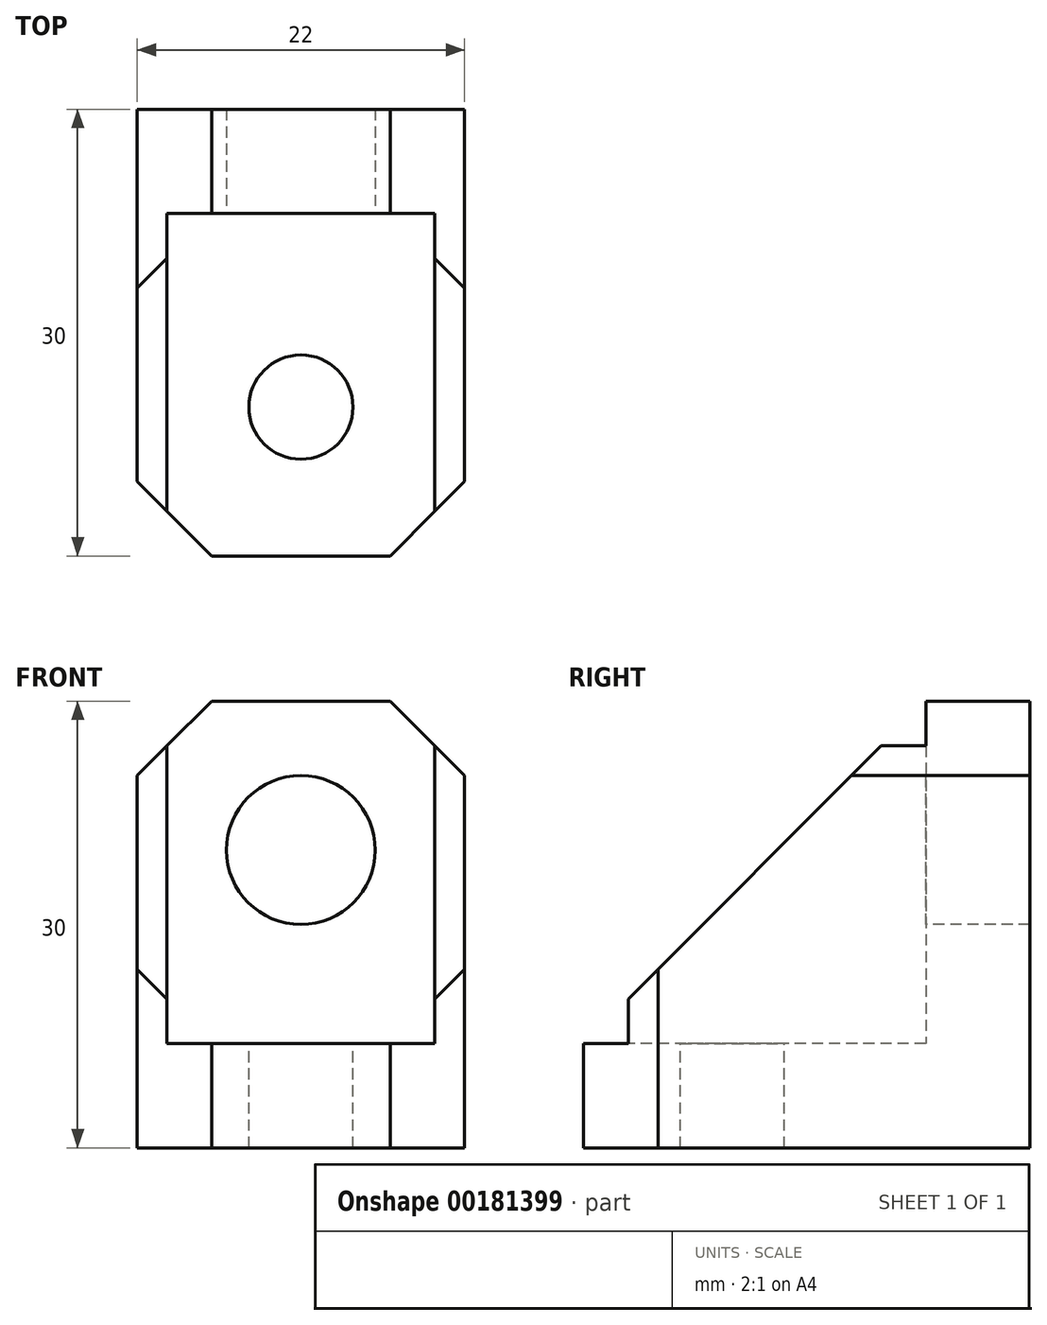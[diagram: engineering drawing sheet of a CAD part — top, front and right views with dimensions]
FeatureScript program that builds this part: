
annotation { "Feature Type Name" : "Feature", "Feature Type Description" : "" }
export const myFeature = defineFeature(function(context is Context, id is Id, definition is map)
    precondition{}
    {
        {
            var Q0;
            Q0=qCreatedBy(makeId("Top.planeOp"),FACE);
            var sketch = newSketch(context, id + "F0", { "sketchPlane" : qUnion([Q0])});
            skLineSegment(sketch, "E0.bottom", {"start": v(11, -15) * mm, "end": v(-11, -15) * mm});
            skLineSegment(sketch, "E0.top", {"start": v(11, 15) * mm, "end": v(-11, 15) * mm});
            skLineSegment(sketch, "E0.left", {"start": v(11, -15) * mm, "end": v(11, 15) * mm});
            skLineSegment(sketch, "E0.right", {"start": v(-11, -15) * mm, "end": v(-11, 15) * mm});
            skPoint(sketch, "E0.middle", {"position": v(0, 0) * mm});
            skLineSegment(sketch, "E1", {"start": v(-11, 8) * mm, "end": v(11, 8) * mm});
            skLineSegment(sketch, "E2", {"start": v(-11, 5) * mm, "end": v(11, 5) * mm, "construction": true});
            skCircle(sketch, "E3", {"center": v(0, -5) * mm, "radius": 3.5 * mm});
            skLineSegment(sketch, "E4", {"start": v(0, 5) * mm, "end": v(0, -15) * mm, "construction": true});
            skLineSegment(sketch, "E5", {"start": v(-9, 8) * mm, "end": v(-9, -15) * mm});
            skLineSegment(sketch, "E6.MirrorCS", {"start": v(9, 8) * mm, "end": v(9, -15) * mm});
            skSolve(sketch);
        }
        {
            var Q0;
            {var subQ3=sQuery(id+"F0.wireOp",EDGE,"E5");Q0=makeQuery(id+"F0.imprint","IMPRINT",FACE,{"disambiguationData":[TD([[makeQuery(id+"F0.imprint","IMPRINT",EDGE,{"derivedFrom":subQ3}),-1.0]])]});}
            var Q1;
            Q1=makeQuery(id+"F0.imprint","IMPRINT",FACE,{"disambiguationData":[TD([[makeQuery(id+"F0.imprint","IMPRINT",EDGE,{"derivedFrom":sQuery(id+"F0.wireOp",EDGE,"E3")}),-1.0]])]});
            var Q2;
            {var subQ3=sQuery(id+"F0.wireOp",EDGE,"E6.MirrorCS");Q2=makeQuery(id+"F0.imprint","IMPRINT",FACE,{"disambiguationData":[TD([[makeQuery(id+"F0.imprint","IMPRINT",EDGE,{"derivedFrom":subQ3}),1.0]])]});}
            var Q3;
            {var subQ4=sQuery(id+"F0.wireOp",EDGE,"E0.top");Q3=makeQuery(id+"F0.imprint","IMPRINT",FACE,{"disambiguationData":[TD([[makeQuery(id+"F0.imprint","IMPRINT",EDGE,{"derivedFrom":subQ4}),1.0]])]});}
            extrude(context, id + "F1", {"entities" : qUnion([Q0, Q1, Q2, Q3]), "oppositeDirection" : true, "depth" : 7 * mm});
        }
        {
            var Q0;
            {var subQ4=sQuery(id+"F0.wireOp",EDGE,"E0.top");Q0=makeQuery(id+"F0.imprint","IMPRINT",FACE,{"disambiguationData":[TD([[makeQuery(id+"F0.imprint","IMPRINT",EDGE,{"derivedFrom":subQ4}),1.0]])]});}
            var Q1;
            {var subQ3=sQuery(id+"F0.wireOp",EDGE,"E5");Q1=makeQuery(id+"F0.imprint","IMPRINT",FACE,{"disambiguationData":[TD([[makeQuery(id+"F0.imprint","IMPRINT",EDGE,{"derivedFrom":subQ3}),-1.0]])]});}
            var Q2;
            {var subQ3=sQuery(id+"F0.wireOp",EDGE,"E6.MirrorCS");Q2=makeQuery(id+"F0.imprint","IMPRINT",FACE,{"disambiguationData":[TD([[makeQuery(id+"F0.imprint","IMPRINT",EDGE,{"derivedFrom":subQ3}),1.0]])]});}
            extrude(context, id + "F2", {"entities" : qUnion([Q0, Q1, Q2]), "operationType" : NewBodyOperationType.ADD, "depth" : 23 * mm});
        }
        {
            var Q0;
            Q0=makeQuery(id+"F2.opExtrude","SWEPT_FACE",FACE,{"disambiguationData":[OSD([sQuery(id+"F0.wireOp",EDGE,"E1")])]});
            var sketch = newSketch(context, id + "F3", { "sketchPlane" : qUnion([Q0])});
            skLineSegment(sketch, "E7", {"start": v(-9, 3) * mm, "end": v(9, 3) * mm, "construction": true});
            skLineSegment(sketch, "E8", {"start": v(0, 3) * mm, "end": v(0, 23) * mm, "construction": true});
            skCircle(sketch, "E9", {"center": v(0, 13) * mm, "radius": 5 * mm});
            skSolve(sketch);
        }
        {
            var Q0;
            Q0=makeQuery(id+"F3.imprint","IMPRINT",FACE,{"disambiguationData":[TD([[makeQuery(id+"F3.imprint","IMPRINT",EDGE,{"derivedFrom":sQuery(id+"F3.wireOp",EDGE,"E9")}),1.0]])]});
            extrude(context, id + "F4", {"entities" : qUnion([Q0]), "operationType" : NewBodyOperationType.REMOVE, "oppositeDirection" : true, "depth" : 25 * mm});
        }
        {
            var Q0;
            {var subQ0=sQuery(id+"F0.wireOp",EDGE,"E0.bottom");Q0=makeQuery(id+"F2.opExtrude","CAP_EDGE",EDGE,{"disambiguationData":[OSD([subQ0]),TDD([makeQuery(id+"F0.imprint","IMPRINT",EDGE,{"disambiguationData":[TD([[makeQuery(id+"F0.imprint","INTERSECT",VERTEX,{"derivedFrom":[subQ0,sQuery(id+"F0.wireOp",EDGE,"E0.left")]}),-1.0]])],"derivedFrom":subQ0})])],"isStart":false});}
            var Q1;
            {var subQ0=sQuery(id+"F0.wireOp",EDGE,"E0.bottom");Q1=makeQuery(id+"F2.opExtrude","CAP_EDGE",EDGE,{"disambiguationData":[OSD([subQ0]),TDD([makeQuery(id+"F0.imprint","IMPRINT",EDGE,{"disambiguationData":[TD([[makeQuery(id+"F0.imprint","INTERSECT",VERTEX,{"derivedFrom":[subQ0,sQuery(id+"F0.wireOp",EDGE,"E0.right")]}),1.0]])],"derivedFrom":subQ0})])],"isStart":false});}
            chamfer(context, id + "F5", {"entities" : qUnion([Q0, Q1]), "width" : 23 * mm, "tangentPropagation" : true});
        }
        {
            var Q0;
            {var subQ0=sQuery(id+"F0.wireOp",EDGE,"E0.right");var subQ1=sQuery(id+"F0.wireOp",EDGE,"E0.bottom");Q0=makeQuery(id+"F2.boolean.opBoolean","MERGE",EDGE,{"derivedFrom":[makeQuery(id+"F1.opExtrude","SWEPT_EDGE",EDGE,{"disambiguationData":[OSD([subQ1,subQ0])]}),makeQuery(id+"F2.opExtrude","SWEPT_EDGE",EDGE,{"disambiguationData":[OSD([subQ1,subQ0])]})]});}
            var Q1;
            {var subQ0=sQuery(id+"F0.wireOp",EDGE,"E0.left");var subQ1=sQuery(id+"F0.wireOp",EDGE,"E0.bottom");Q1=makeQuery(id+"F2.boolean.opBoolean","MERGE",EDGE,{"derivedFrom":[makeQuery(id+"F1.opExtrude","SWEPT_EDGE",EDGE,{"disambiguationData":[OSD([subQ1,subQ0])]}),makeQuery(id+"F2.opExtrude","SWEPT_EDGE",EDGE,{"disambiguationData":[OSD([subQ1,subQ0])]})]});}
            var Q2;
            Q2=makeQuery(id+"F2.opExtrude","CAP_EDGE",EDGE,{"disambiguationData":[OSD([sQuery(id+"F0.wireOp",EDGE,"E0.right")])],"isStart":false});
            var Q3;
            Q3=makeQuery(id+"F2.opExtrude","CAP_EDGE",EDGE,{"disambiguationData":[OSD([sQuery(id+"F0.wireOp",EDGE,"E0.left")])],"isStart":false});
            chamfer(context, id + "F6", {"entities" : qUnion([Q0, Q1, Q2, Q3]), "width" : 5 * mm, "tangentPropagation" : true});
        }
    });
